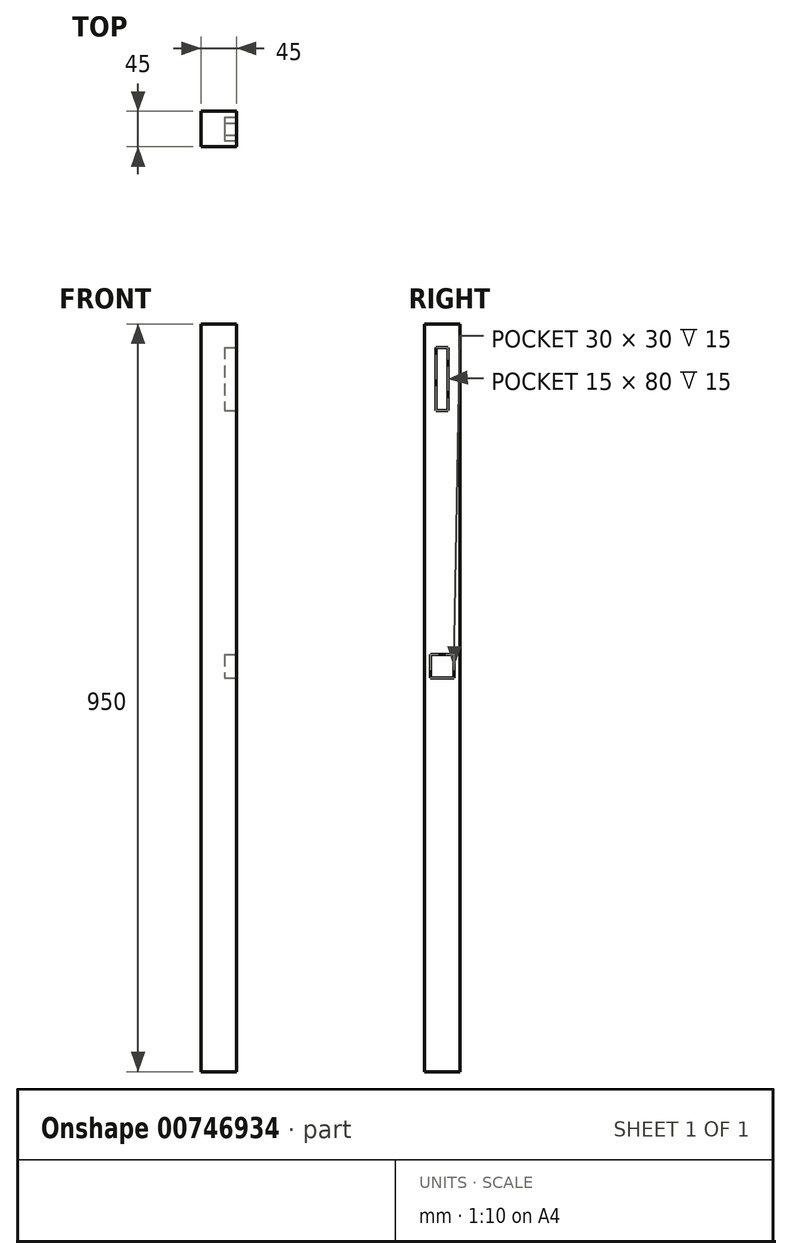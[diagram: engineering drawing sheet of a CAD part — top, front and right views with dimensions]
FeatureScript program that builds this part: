
annotation { "Feature Type Name" : "Feature", "Feature Type Description" : "" }
export const myFeature = defineFeature(function(context is Context, id is Id, definition is map)
    precondition{}
    {
        {
            var Q0;
            Q0=qCreatedBy(makeId("Top.planeOp"),FACE);
            var sketch = newSketch(context, id + "F0", { "sketchPlane" : qUnion([Q0])});
            skLineSegment(sketch, "E0.bottom", {"start": v(22.5, 22.5) * mm, "end": v(-22.5, 22.5) * mm});
            skLineSegment(sketch, "E0.top", {"start": v(22.5, -22.5) * mm, "end": v(-22.5, -22.5) * mm});
            skLineSegment(sketch, "E0.left", {"start": v(22.5, 22.5) * mm, "end": v(22.5, -22.5) * mm});
            skLineSegment(sketch, "E0.right", {"start": v(-22.5, 22.5) * mm, "end": v(-22.5, -22.5) * mm});
            skPoint(sketch, "E0.middle", {"position": v(0, 0) * mm});
            skSolve(sketch);
        }
        {
            var Q0;
            Q0=qSketchRegion(id+"F0",true);
            extrude(context, id + "F1", {"entities" : qUnion([Q0]), "endBound" : BoundingType.SYMMETRIC, "depth" : 950 * mm, "offsetDistance" : 25 * mm});
        }
        {
            var Q0;
            Q0=makeQuery(id+"F1.opExtrude","SWEPT_FACE",FACE,{"disambiguationData":[OSD([sQuery(id+"F0.wireOp",EDGE,"E0.left")])]});
            var sketch = newSketch(context, id + "F2", { "sketchPlane" : qUnion([Q0])});
            skLineSegment(sketch, "E1.bottom", {"start": v(7.5, 445) * mm, "end": v(-7.5, 445) * mm});
            skLineSegment(sketch, "E1.top", {"start": v(7.5, 365) * mm, "end": v(-7.5, 365) * mm});
            skLineSegment(sketch, "E1.left", {"start": v(7.5, 445) * mm, "end": v(7.5, 365) * mm});
            skLineSegment(sketch, "E1.right", {"start": v(-7.5, 445) * mm, "end": v(-7.5, 365) * mm});
            skPoint(sketch, "E1.middle", {"position": v(0, 405) * mm});
            skLineSegment(sketch, "E2.bottom", {"start": v(15, 55) * mm, "end": v(-15, 55) * mm});
            skLineSegment(sketch, "E2.top", {"start": v(15, 25) * mm, "end": v(-15, 25) * mm});
            skLineSegment(sketch, "E2.left", {"start": v(15, 55) * mm, "end": v(15, 25) * mm});
            skLineSegment(sketch, "E2.right", {"start": v(-15, 55) * mm, "end": v(-15, 25) * mm});
            skPoint(sketch, "E2.middle", {"position": v(0, 40) * mm});
            skSolve(sketch);
        }
        {
            var Q0;
            Q0=qSketchRegion(id+"F2",true);
            extrude(context, id + "F3", {"entities" : qUnion([Q0]), "operationType" : NewBodyOperationType.REMOVE, "oppositeDirection" : true, "depth" : 15 * mm, "offsetDistance" : 25 * mm});
        }
    });
